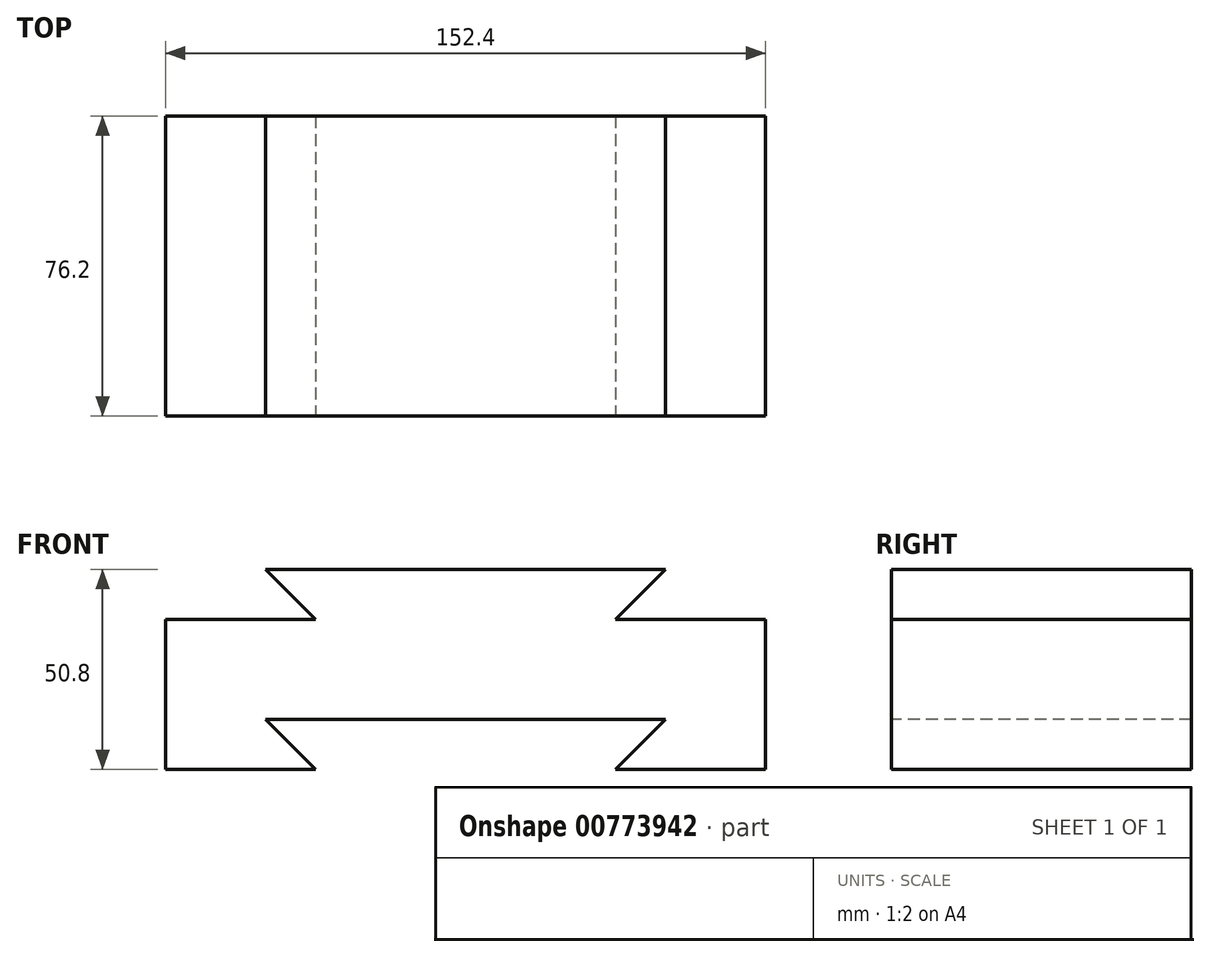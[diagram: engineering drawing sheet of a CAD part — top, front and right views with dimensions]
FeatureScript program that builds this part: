
annotation { "Feature Type Name" : "Feature", "Feature Type Description" : "" }
export const myFeature = defineFeature(function(context is Context, id is Id, definition is map)
    precondition{}
    {
        {
            var Q0;
            Q0=qCreatedBy(makeId("Front.planeOp"),FACE);
            var sketch = newSketch(context, id + "F0", { "sketchPlane" : qUnion([Q0])});
            skLineSegment(sketch, "E0", {"start": v(0, 0) * mm, "end": v(152.4, 0) * mm});
            skLineSegment(sketch, "E1", {"start": v(152.4, 0) * mm, "end": v(152.4, 50.8) * mm});
            skLineSegment(sketch, "E2", {"start": v(152.4, 50.8) * mm, "end": v(0, 50.8) * mm});
            skLineSegment(sketch, "E3", {"start": v(0, 50.8) * mm, "end": v(0, 0) * mm});
            skSolve(sketch);
        }
        {
            var Q0;
            Q0=makeQuery(id+"F0.imprint","IMPRINT",FACE,{"disambiguationData":[TD([[makeQuery(id+"F0.imprint","IMPRINT",EDGE,{"derivedFrom":sQuery(id+"F0.wireOp",EDGE,"E0")}),1.0]])]});
            extrude(context, id + "F1", {"entities" : qUnion([Q0]), "depth" : 76.2 * mm, "offsetDistance" : 25.4 * mm});
        }
        {
            var Q0;
            Q0=makeQuery(id+"F1.opExtrude","CAP_FACE",FACE,{"disambiguationData":[OSD([sQuery(id+"F0.wireOp",EDGE,"E0"),sQuery(id+"F0.wireOp",EDGE,"E1"),sQuery(id+"F0.wireOp",EDGE,"E2"),sQuery(id+"F0.wireOp",EDGE,"E3")])],"isStart":false});
            var sketch = newSketch(context, id + "F2", { "sketchPlane" : qUnion([Q0])});
            skLineSegment(sketch, "E4", {"start": v(152.4, 50.8) * mm, "end": v(127, 50.8) * mm});
            skLineSegment(sketch, "E5", {"start": v(152.4, 50.8) * mm, "end": v(152.4, 38.1) * mm});
            skLineSegment(sketch, "E6", {"start": v(152.4, 38.1) * mm, "end": v(114.3, 38.1) * mm});
            skLineSegment(sketch, "E7", {"start": v(114.3, 38.1) * mm, "end": v(127, 50.8) * mm});
            skLineSegment(sketch, "E8", {"start": v(152.4, 38.1) * mm, "end": v(152.4, 50.8) * mm});
            skSolve(sketch);
        }
        {
            var Q0;
            Q0=makeQuery(id+"F2.imprint","IMPRINT",FACE,{"disambiguationData":[TD([[makeQuery(id+"F2.imprint","IMPRINT",EDGE,{"derivedFrom":sQuery(id+"F2.wireOp",EDGE,"E4")}),1.0]])]});
            extrude(context, id + "F3", {"entities" : qUnion([Q0]), "operationType" : NewBodyOperationType.REMOVE, "oppositeDirection" : true, "depth" : 76.2 * mm, "offsetDistance" : 25.4 * mm});
        }
        {
            var Q0;
            Q0=makeQuery(id+"F1.opExtrude","CAP_FACE",FACE,{"disambiguationData":[OSD([sQuery(id+"F0.wireOp",EDGE,"E0"),sQuery(id+"F0.wireOp",EDGE,"E1"),sQuery(id+"F0.wireOp",EDGE,"E2"),sQuery(id+"F0.wireOp",EDGE,"E3")])],"isStart":false});
            var sketch = newSketch(context, id + "F4", { "sketchPlane" : qUnion([Q0])});
            skLineSegment(sketch, "E9", {"start": v(0, 50.8) * mm, "end": v(0, 38.1) * mm});
            skLineSegment(sketch, "E10", {"start": v(0, 50.8) * mm, "end": v(25.4, 50.8) * mm});
            skLineSegment(sketch, "E11", {"start": v(0, 38.1) * mm, "end": v(38.1, 38.1) * mm});
            skLineSegment(sketch, "E12", {"start": v(38.1, 38.1) * mm, "end": v(25.4, 50.8) * mm});
            skSolve(sketch);
        }
        {
            var Q0;
            Q0=makeQuery(id+"F4.imprint","IMPRINT",FACE,{"disambiguationData":[TD([[makeQuery(id+"F4.imprint","IMPRINT",EDGE,{"derivedFrom":sQuery(id+"F4.wireOp",EDGE,"E9")}),1.0]])]});
            extrude(context, id + "F5", {"entities" : qUnion([Q0]), "operationType" : NewBodyOperationType.REMOVE, "oppositeDirection" : true, "depth" : 76.2 * mm, "offsetDistance" : 25.4 * mm});
        }
        {
            var Q0;
            Q0=makeQuery(id+"F1.opExtrude","CAP_FACE",FACE,{"disambiguationData":[OSD([sQuery(id+"F0.wireOp",EDGE,"E0"),sQuery(id+"F0.wireOp",EDGE,"E1"),sQuery(id+"F0.wireOp",EDGE,"E2"),sQuery(id+"F0.wireOp",EDGE,"E3")])],"isStart":false});
            var sketch = newSketch(context, id + "F6", { "sketchPlane" : qUnion([Q0])});
            skLineSegment(sketch, "E13", {"start": v(25.4, 12.7) * mm, "end": v(38.1, 0) * mm});
            skLineSegment(sketch, "E14", {"start": v(25.4, 12.7) * mm, "end": v(127, 12.7) * mm});
            skLineSegment(sketch, "E15", {"start": v(114.3, 0) * mm, "end": v(127, 12.7) * mm});
            skLineSegment(sketch, "E16", {"start": v(114.3, 0) * mm, "end": v(38.1, 0) * mm});
            skSolve(sketch);
        }
        {
            var Q0;
            Q0=makeQuery(id+"F6.imprint","IMPRINT",FACE,{"disambiguationData":[TD([[makeQuery(id+"F6.imprint","IMPRINT",EDGE,{"derivedFrom":sQuery(id+"F6.wireOp",EDGE,"E13")}),1.0]])]});
            extrude(context, id + "F7", {"entities" : qUnion([Q0]), "operationType" : NewBodyOperationType.REMOVE, "oppositeDirection" : true, "depth" : 76.2 * mm, "offsetDistance" : 25.4 * mm});
        }
    });
